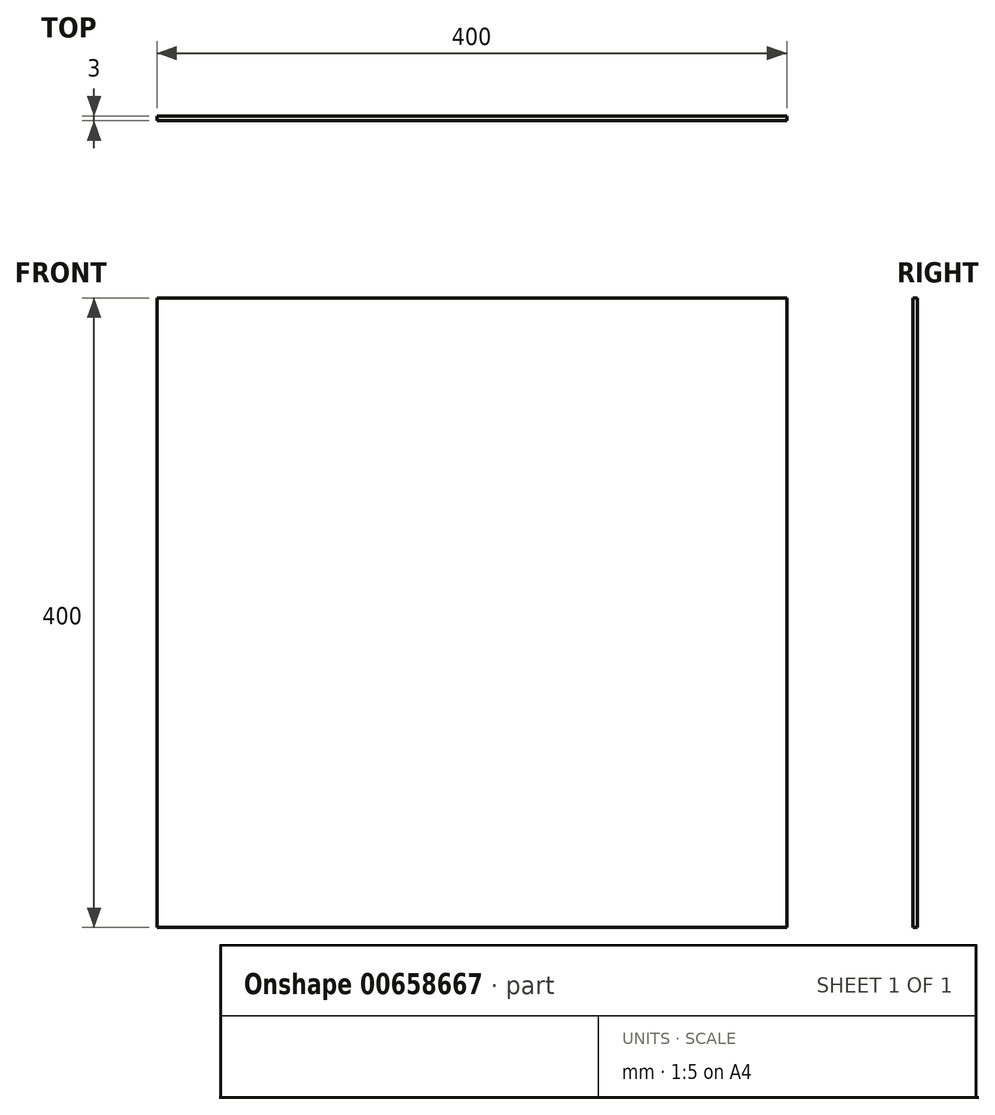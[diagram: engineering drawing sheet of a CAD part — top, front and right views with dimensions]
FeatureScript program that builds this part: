
annotation { "Feature Type Name" : "Feature", "Feature Type Description" : "" }
export const myFeature = defineFeature(function(context is Context, id is Id, definition is map)
    precondition{}
    {
        {
            var Q0;
            Q0=qCreatedBy(makeId("Front.planeOp"),FACE);
            var sketch = newSketch(context, id + "F0", { "sketchPlane" : qUnion([Q0])});
            skLineSegment(sketch, "E0.bottom", {"start": v(200, -200) * mm, "end": v(-200, -200) * mm});
            skLineSegment(sketch, "E0.top", {"start": v(200, 200) * mm, "end": v(-200, 200) * mm});
            skLineSegment(sketch, "E0.left", {"start": v(200, -200) * mm, "end": v(200, 200) * mm});
            skLineSegment(sketch, "E0.right", {"start": v(-200, -200) * mm, "end": v(-200, 200) * mm});
            skPoint(sketch, "E0.middle", {"position": v(0, 0) * mm});
            skSolve(sketch);
        }
        {
            var Q0;
            Q0=makeQuery(id+"F0.imprint","IMPRINT",FACE,{"disambiguationData":[TD([[makeQuery(id+"F0.imprint","IMPRINT",EDGE,{"derivedFrom":sQuery(id+"F0.wireOp",EDGE,"E0.bottom")}),-1.0]])]});
            extrude(context, id + "F1", {"entities" : qUnion([Q0]), "depth" : 3 * mm, "offsetDistance" : 25 * mm});
        }
    });
